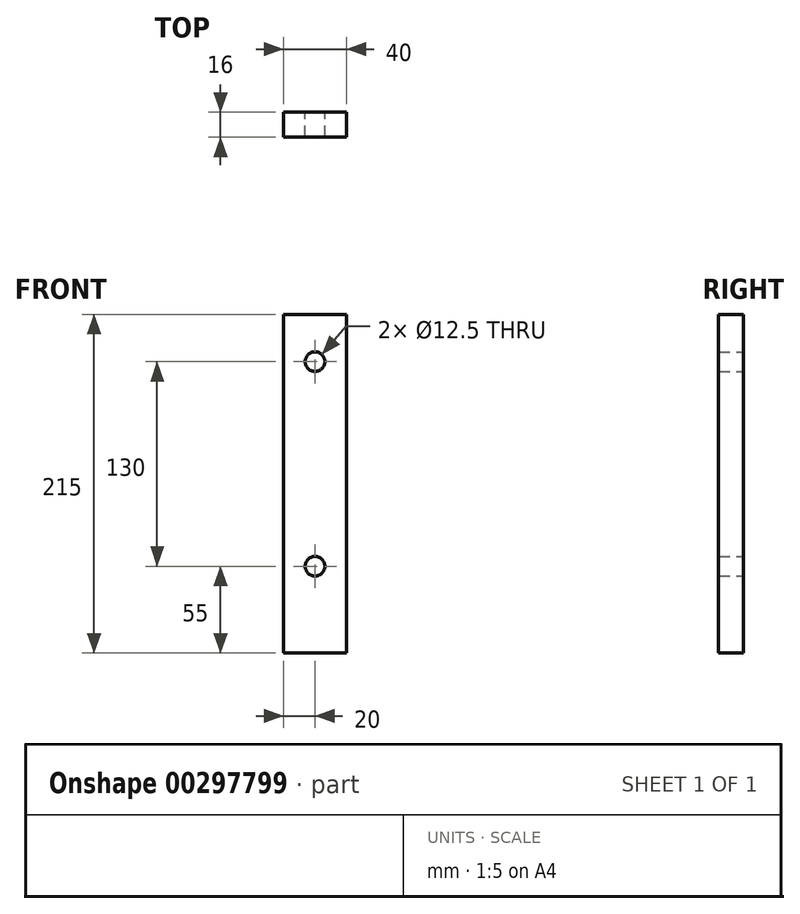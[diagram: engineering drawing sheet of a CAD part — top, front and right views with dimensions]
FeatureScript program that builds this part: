
annotation { "Feature Type Name" : "Feature", "Feature Type Description" : "" }
export const myFeature = defineFeature(function(context is Context, id is Id, definition is map)
    precondition{}
    {
        {
            var Q0;
            Q0=qCreatedBy(makeId("Front.planeOp"),FACE);
            var sketch = newSketch(context, id + "F0", { "sketchPlane" : qUnion([Q0])});
            skLineSegment(sketch, "E0.bottom", {"start": v(-20, 95) * mm, "end": v(20, 95) * mm});
            skLineSegment(sketch, "E0.top", {"start": v(-20, -120) * mm, "end": v(20, -120) * mm});
            skLineSegment(sketch, "E0.left", {"start": v(-20, 95) * mm, "end": v(-20, -120) * mm});
            skLineSegment(sketch, "E0.right", {"start": v(20, 95) * mm, "end": v(20, -120) * mm});
            skPoint(sketch, "E0.middle", {"position": v(0, 0) * mm});
            skCircle(sketch, "E1", {"center": v(0, 65) * mm, "radius": 6.25 * mm});
            skCircle(sketch, "E2.MirrorC", {"center": v(0, -65) * mm, "radius": 6.25 * mm});
            skSolve(sketch);
        }
        {
            var Q0;
            Q0 = qSketchRegion(id + "F0", true);
            extrude(context, id + "F1", {"entities" : qUnion([Q0]), "depth" : 16 * mm});
        }
    });
